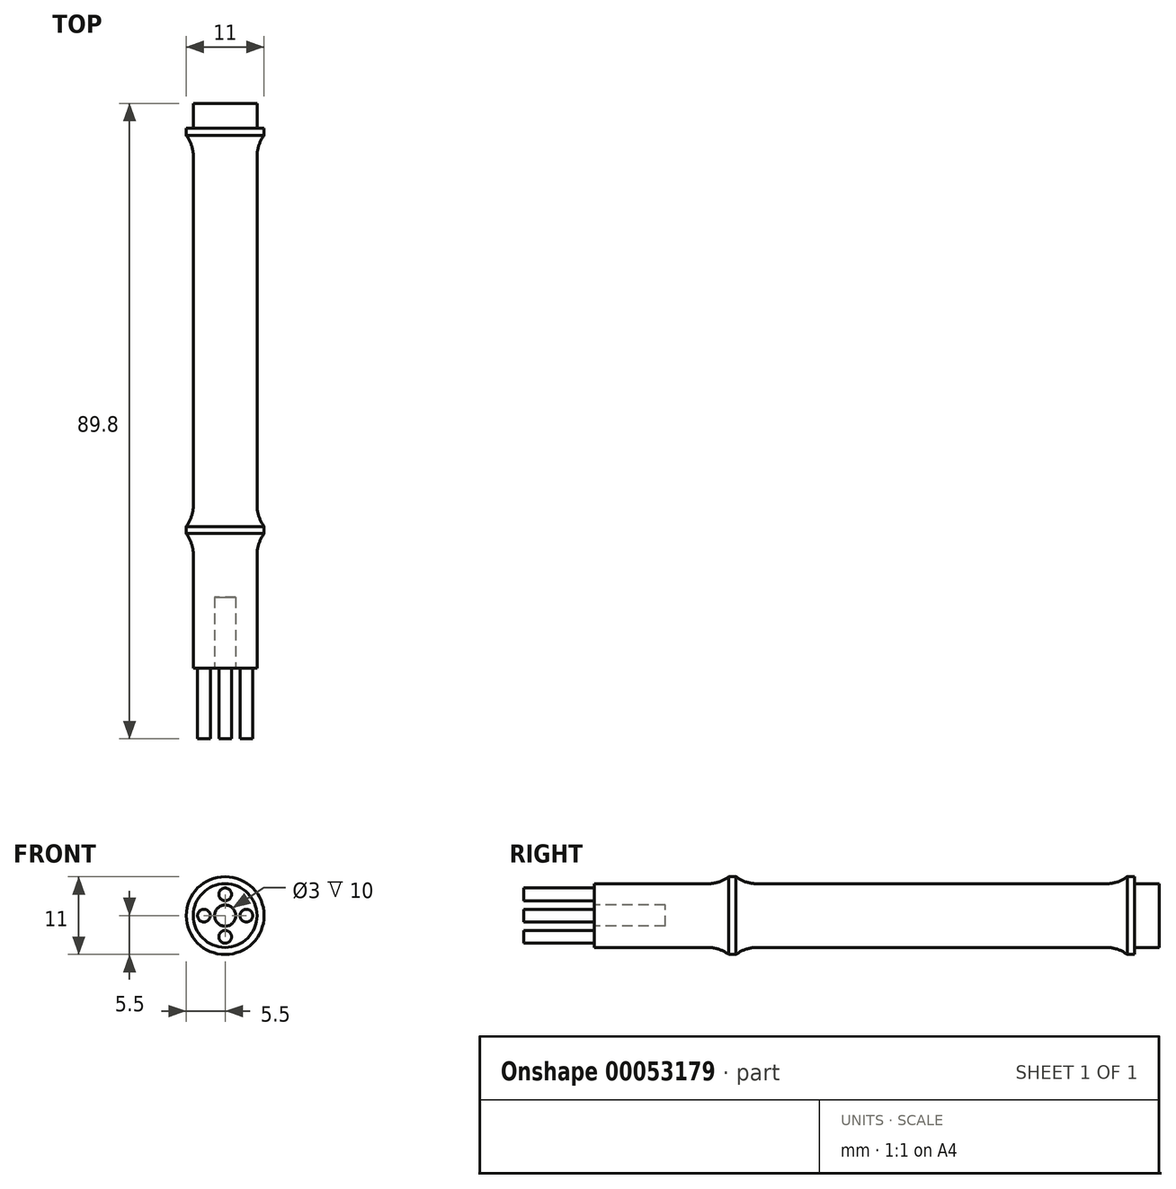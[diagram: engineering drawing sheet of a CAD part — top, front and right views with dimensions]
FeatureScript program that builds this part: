
annotation { "Feature Type Name" : "Feature", "Feature Type Description" : "" }
export const myFeature = defineFeature(function(context is Context, id is Id, definition is map)
    precondition{}
    {
        {
            var Q0;
            Q0=qCreatedBy(makeId("Front.planeOp"),FACE);
            var sketch = newSketch(context, id + "F0", { "sketchPlane" : qUnion([Q0])});
            skCircle(sketch, "E0", {"center": v(0, 0) * mm, "radius": 4.5 * mm});
            skSolve(sketch);
        }
        {
            var Q0;
            Q0=makeQuery(id+"F0.imprint","IMPRINT",FACE,{"disambiguationData":[TD([[makeQuery(id+"F0.imprint","IMPRINT",EDGE,{"derivedFrom":sQuery(id+"F0.wireOp",EDGE,"E0")}),1.0]])]});
            extrude(context, id + "F1", {"entities" : qUnion([Q0]), "depth" : 19 * mm});
        }
        {
            var Q0;
            Q0=makeQuery(id+"F1.opExtrude","CAP_FACE",FACE,{"disambiguationData":[OSD([sQuery(id+"F0.wireOp",EDGE,"E0")])],"isStart":true});
            extrude(context, id + "F2", {"entities" : qUnion([Q0]), "operationType" : NewBodyOperationType.ADD, "depth" : 57.3 * mm});
        }
        {
            var Q0;
            Q0=qCreatedBy(makeId("Front.planeOp"),FACE);
            var sketch = newSketch(context, id + "F3", { "sketchPlane" : qUnion([Q0])});
            skCircle(sketch, "E1", {"center": v(0, 0) * mm, "radius": 5.5 * mm});
            skSolve(sketch);
        }
        {
            var Q0;
            Q0=makeQuery(id+"F3.imprint","IMPRINT",FACE,{"disambiguationData":[TD([[makeQuery(id+"F3.imprint","IMPRINT",EDGE,{"derivedFrom":sQuery(id+"F3.wireOp",EDGE,"E1")}),1.0]])]});
            extrude(context, id + "F4", {"entities" : qUnion([Q0]), "operationType" : NewBodyOperationType.ADD, "oppositeDirection" : true, "depth" : 1 * mm});
        }
        {
            var Q0;
            {var subQ0=sQuery(id+"F0.wireOp",EDGE,"E0");Q0=makeQuery(id+"F4.boolean.opBoolean","INTERSECT",EDGE,{"derivedFrom":[makeQuery(id+"F2.boolean.opBoolean","MERGE",FACE,{"derivedFrom":[makeQuery(id+"F1.opExtrude","SWEPT_FACE",FACE,{"disambiguationData":[OSD([subQ0])]}),makeQuery(id+"F2.opExtrude","SWEPT_FACE",FACE,{"disambiguationData":[OSD([subQ0])]})]}),makeQuery(id+"F4.opExtrude","CAP_FACE",FACE,{"disambiguationData":[OSD([sQuery(id+"F3.wireOp",EDGE,"E1")])],"isStart":true})]});}
            var Q1;
            {var subQ0=sQuery(id+"F0.wireOp",EDGE,"E0");Q1=makeQuery(id+"F4.boolean.opBoolean","INTERSECT",EDGE,{"derivedFrom":[makeQuery(id+"F2.boolean.opBoolean","MERGE",FACE,{"derivedFrom":[makeQuery(id+"F1.opExtrude","SWEPT_FACE",FACE,{"disambiguationData":[OSD([subQ0])]}),makeQuery(id+"F2.opExtrude","SWEPT_FACE",FACE,{"disambiguationData":[OSD([subQ0])]})]}),makeQuery(id+"F4.opExtrude","CAP_FACE",FACE,{"disambiguationData":[OSD([sQuery(id+"F3.wireOp",EDGE,"E1")])],"isStart":false})]});}
            fillet(context, id + "F5", {"entities" : qUnion([Q0, Q1]), "radius" : 5 * mm, "tangentPropagation" : true, "allowEdgeOverflow" : false});
        }
        {
            var Q0;
            Q0=makeQuery(id+"F1.opExtrude","CAP_FACE",FACE,{"disambiguationData":[OSD([sQuery(id+"F0.wireOp",EDGE,"E0")])],"isStart":false});
            var sketch = newSketch(context, id + "F6", { "sketchPlane" : qUnion([Q0])});
            skCircle(sketch, "E2", {"center": v(0, 0) * mm, "radius": 1.5 * mm});
            skSolve(sketch);
        }
        {
            var Q0;
            Q0=makeQuery(id+"F6.imprint","IMPRINT",FACE,{"disambiguationData":[TD([[makeQuery(id+"F6.imprint","IMPRINT",EDGE,{"derivedFrom":sQuery(id+"F6.wireOp",EDGE,"E2")}),1.0]])]});
            extrude(context, id + "F7", {"entities" : qUnion([Q0]), "operationType" : NewBodyOperationType.REMOVE, "oppositeDirection" : true, "depth" : 10 * mm});
        }
        {
            var Q0;
            Q0=makeQuery(id+"F1.opExtrude","CAP_FACE",FACE,{"disambiguationData":[OSD([sQuery(id+"F0.wireOp",EDGE,"E0")])],"isStart":false});
            var sketch = newSketch(context, id + "F8", { "sketchPlane" : qUnion([Q0])});
            skCircle(sketch, "E3", {"center": v(-3, 0) * mm, "radius": 0.9 * mm});
            skCircle(sketch, "E4", {"center": v(0, -3) * mm, "radius": 0.9 * mm});
            skCircle(sketch, "E5", {"center": v(3, 0) * mm, "radius": 0.9 * mm});
            skCircle(sketch, "E6", {"center": v(0, 3) * mm, "radius": 0.9 * mm});
            skSolve(sketch);
        }
        {
            var Q0;
            Q0 = qSketchRegion(id + "F8", true);
            extrude(context, id + "F9", {"entities" : qUnion([Q0]), "operationType" : NewBodyOperationType.ADD, "depth" : 10 * mm});
        }
        {
            var Q0;
            Q0=makeQuery(id+"F2.opExtrude","CAP_FACE",FACE,{"disambiguationData":[OSD([sQuery(id+"F0.wireOp",EDGE,"E0")])],"isStart":false});
            var sketch = newSketch(context, id + "F10", { "sketchPlane" : qUnion([Q0])});
            skCircle(sketch, "E7", {"center": v(0, 0) * mm, "radius": 4.5 * mm});
            skSolve(sketch);
        }
        {
            var Q0;
            Q0=makeQuery(id+"F10.imprint","IMPRINT",FACE,{"disambiguationData":[TD([[makeQuery(id+"F10.imprint","IMPRINT",EDGE,{"derivedFrom":sQuery(id+"F10.wireOp",EDGE,"E7")}),-1.0]])]});
            var sketch = newSketch(context, id + "F11", { "sketchPlane" : qUnion([Q0])});
            skCircle(sketch, "E8", {"center": v(0, 0) * mm, "radius": 5.5 * mm});
            skSolve(sketch);
        }
        {
            var Q0;
            Q0=makeQuery(id+"F10.imprint","IMPRINT",FACE,{"disambiguationData":[TD([[makeQuery(id+"F10.imprint","IMPRINT",EDGE,{"derivedFrom":sQuery(id+"F10.wireOp",EDGE,"E7")}),-1.0]])]});
            extrude(context, id + "F12", {"entities" : qUnion([Q0]), "operationType" : NewBodyOperationType.ADD, "depth" : 3.5 * mm});
        }
        {
            var Q0;
            Q0=makeQuery(id+"F11.imprint","IMPRINT",FACE,{"disambiguationData":[TD([[makeQuery(id+"F11.imprint","IMPRINT",EDGE,{"derivedFrom":sQuery(id+"F11.wireOp",EDGE,"E8")}),1.0]])]});
            extrude(context, id + "F13", {"entities" : qUnion([Q0]), "operationType" : NewBodyOperationType.ADD, "oppositeDirection" : true, "depth" : 1 * mm});
        }
        {
            var Q0;
            Q0=makeQuery(id+"F13.opExtrude","CAP_EDGE",EDGE,{"disambiguationData":[OSD([sQuery(id+"F10.wireOp",EDGE,"E7")])],"isStart":false});
            fillet(context, id + "F14", {"entities" : qUnion([Q0]), "radius" : 5 * mm, "tangentPropagation" : true, "allowEdgeOverflow" : false});
        }
    });
